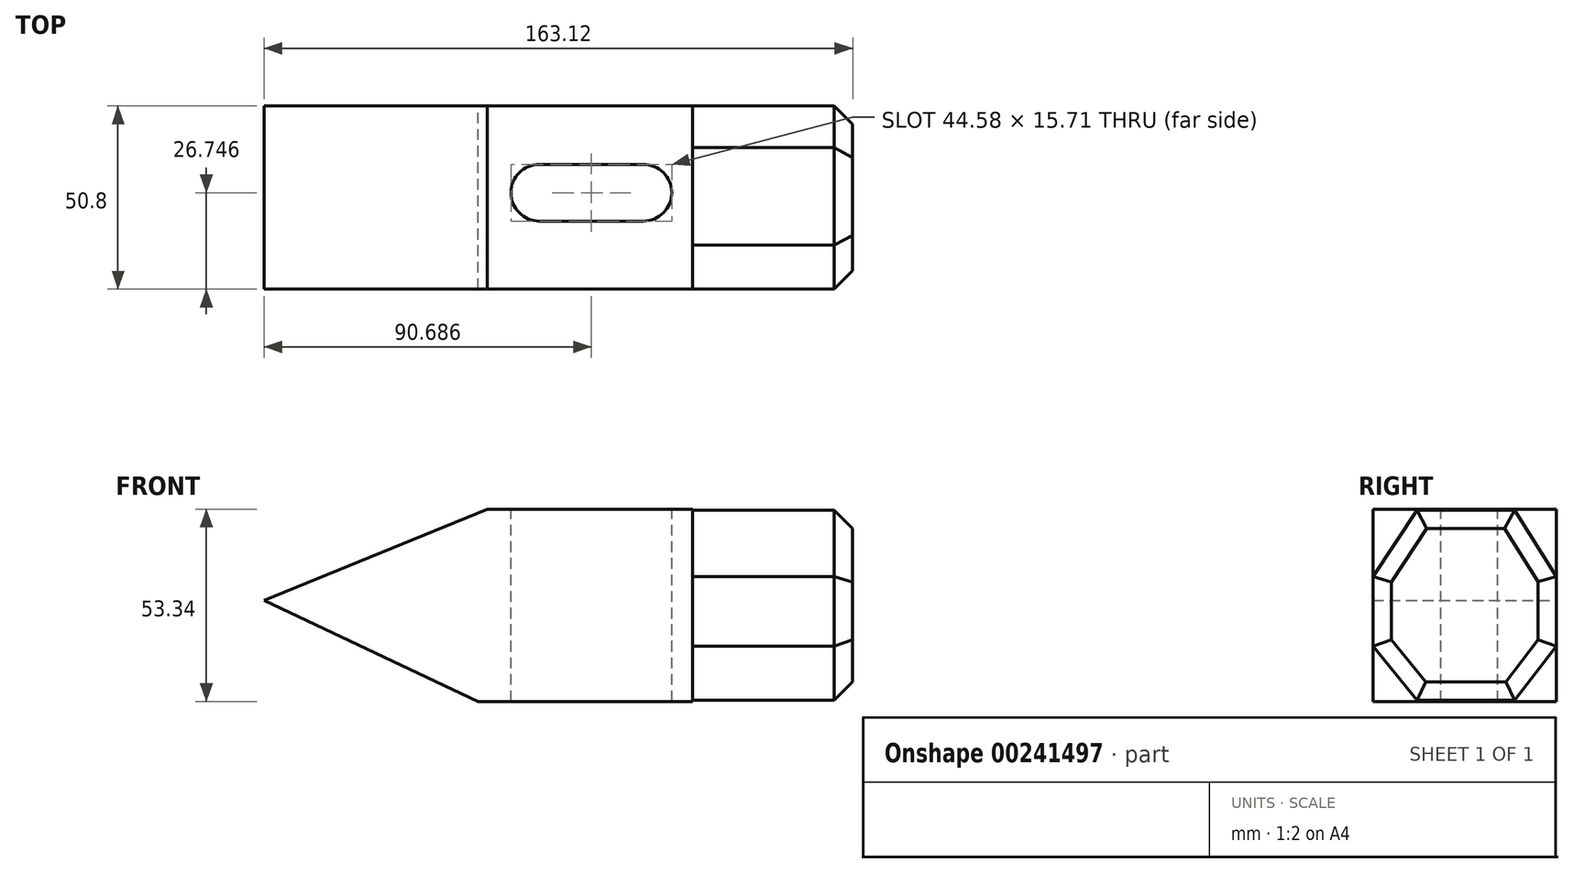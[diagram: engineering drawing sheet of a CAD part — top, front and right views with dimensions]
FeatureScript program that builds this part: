
annotation { "Feature Type Name" : "Feature", "Feature Type Description" : "" }
export const myFeature = defineFeature(function(context is Context, id is Id, definition is map)
    precondition{}
    {
        {
            var Q0;
            Q0=qCreatedBy(makeId("Front.planeOp"),FACE);
            var sketch = newSketch(context, id + "F0", { "sketchPlane" : qUnion([Q0])});
            skLineSegment(sketch, "E0", {"start": v(-76.25, 0) * mm, "end": v(-14.4, 25.36) * mm});
            skLineSegment(sketch, "E1", {"start": v(-76.25, 0) * mm, "end": v(-17.02, -27.98) * mm});
            skLineSegment(sketch, "E2", {"start": v(-14.4, 25.36) * mm, "end": v(42.54, 25.36) * mm});
            skLineSegment(sketch, "E3", {"start": v(-17.02, -27.98) * mm, "end": v(42.54, -27.98) * mm});
            skLineSegment(sketch, "E4", {"start": v(42.54, 25.36) * mm, "end": v(42.54, -27.98) * mm});
            skSolve(sketch);
        }
        {
            var Q0;
            Q0=makeQuery(id+"F0.imprint","IMPRINT",FACE,{"disambiguationData":[TD([[makeQuery(id+"F0.imprint","IMPRINT",EDGE,{"derivedFrom":sQuery(id+"F0.wireOp",EDGE,"E0")}),-1.0]])]});
            extrude(context, id + "F1", {"entities" : qUnion([Q0]), "depth" : 50.8 * mm});
        }
        {
            var Q0;
            Q0=qCreatedBy(makeId("Right.planeOp"),FACE);
            var sketch = newSketch(context, id + "F2", { "sketchPlane" : qUnion([Q0])});
            skLineSegment(sketch, "E5", {"start": v(-38.61, 25.03) * mm, "end": v(-11.45, 25.03) * mm});
            skLineSegment(sketch, "E6", {"start": v(-11.45, 25.03) * mm, "end": v(0, 6.7) * mm});
            skLineSegment(sketch, "E7", {"start": v(0, 6.7) * mm, "end": v(0, -12.6) * mm});
            skLineSegment(sketch, "E8", {"start": v(0, -12.6) * mm, "end": v(-11.45, -27.65) * mm});
            skLineSegment(sketch, "E9", {"start": v(-11.45, -27.65) * mm, "end": v(-38.61, -27.65) * mm});
            skLineSegment(sketch, "E10", {"start": v(-38.61, -27.65) * mm, "end": v(-50.72, -12.6) * mm});
            skLineSegment(sketch, "E11", {"start": v(-50.72, -12.6) * mm, "end": v(-50.72, 6.7) * mm});
            skLineSegment(sketch, "E12", {"start": v(-50.72, 6.7) * mm, "end": v(-38.61, 25.03) * mm});
            skSolve(sketch);
        }
        {
            var Q0;
            Q0 = qSketchRegion(id + "F2", true);
            extrude(context, id + "F3", {"entities" : qUnion([Q0]), "operationType" : NewBodyOperationType.ADD, "depth" : 86.87 * mm});
        }
        {
            var Q0;
            Q0=makeQuery(id+"F1.opExtrude","SWEPT_FACE",FACE,{"disambiguationData":[OSD([sQuery(id+"F0.wireOp",EDGE,"E2")])]});
            var sketch = newSketch(context, id + "F4", { "sketchPlane" : qUnion([Q0])});
            skLineSegment(sketch, "E13", {"start": v(0, -16.2) * mm, "end": v(28.87, -16.2) * mm});
            skLineSegment(sketch, "E14", {"start": v(0, -31.9) * mm, "end": v(28.87, -31.9) * mm});
            skArc(sketch, "E15", {"start": v(28.87, -31.9) * mm, "mid": v(36.73, -24.05) * mm, "end": v(28.87, -16.2) * mm});
            skArc(sketch, "E16", {"start": v(0, -16.2) * mm, "mid": v(-7.85, -24.05) * mm, "end": v(0, -31.9) * mm});
            skSolve(sketch);
        }
        {
            var Q0;
            Q0 = qSketchRegion(id + "F4", true);
            extrude(context, id + "F5", {"entities" : qUnion([Q0]), "operationType" : NewBodyOperationType.REMOVE, "oppositeDirection" : true, "depth" : 97.03 * mm});
        }
        {
            var Q0;
            Q0=makeQuery(id+"F3.opExtrude","CAP_EDGE",EDGE,{"disambiguationData":[OSD([sQuery(id+"F2.wireOp",EDGE,"E5")])],"isStart":false});
            var Q1;
            Q1=makeQuery(id+"F3.opExtrude","CAP_EDGE",EDGE,{"disambiguationData":[OSD([sQuery(id+"F2.wireOp",EDGE,"E6")])],"isStart":false});
            var Q2;
            Q2=makeQuery(id+"F3.opExtrude","CAP_EDGE",EDGE,{"disambiguationData":[OSD([sQuery(id+"F2.wireOp",EDGE,"E7")])],"isStart":false});
            var Q3;
            Q3=makeQuery(id+"F3.opExtrude","CAP_EDGE",EDGE,{"disambiguationData":[OSD([sQuery(id+"F2.wireOp",EDGE,"E8")])],"isStart":false});
            var Q4;
            Q4=makeQuery(id+"F3.opExtrude","CAP_EDGE",EDGE,{"disambiguationData":[OSD([sQuery(id+"F2.wireOp",EDGE,"E9")])],"isStart":false});
            var Q5;
            Q5=makeQuery(id+"F3.opExtrude","CAP_FACE",FACE,{"disambiguationData":[OSD([sQuery(id+"F2.wireOp",EDGE,"E5"),sQuery(id+"F2.wireOp",EDGE,"E6"),sQuery(id+"F2.wireOp",EDGE,"E7"),sQuery(id+"F2.wireOp",EDGE,"E8"),sQuery(id+"F2.wireOp",EDGE,"E9"),sQuery(id+"F2.wireOp",EDGE,"E10"),sQuery(id+"F2.wireOp",EDGE,"E11"),sQuery(id+"F2.wireOp",EDGE,"E12")])],"isStart":false});
            chamfer(context, id + "F6", {"entities" : qUnion([Q0, Q1, Q2, Q3, Q4, Q5]), "width" : 5.08 * mm, "tangentPropagation" : true});
        }
    });
